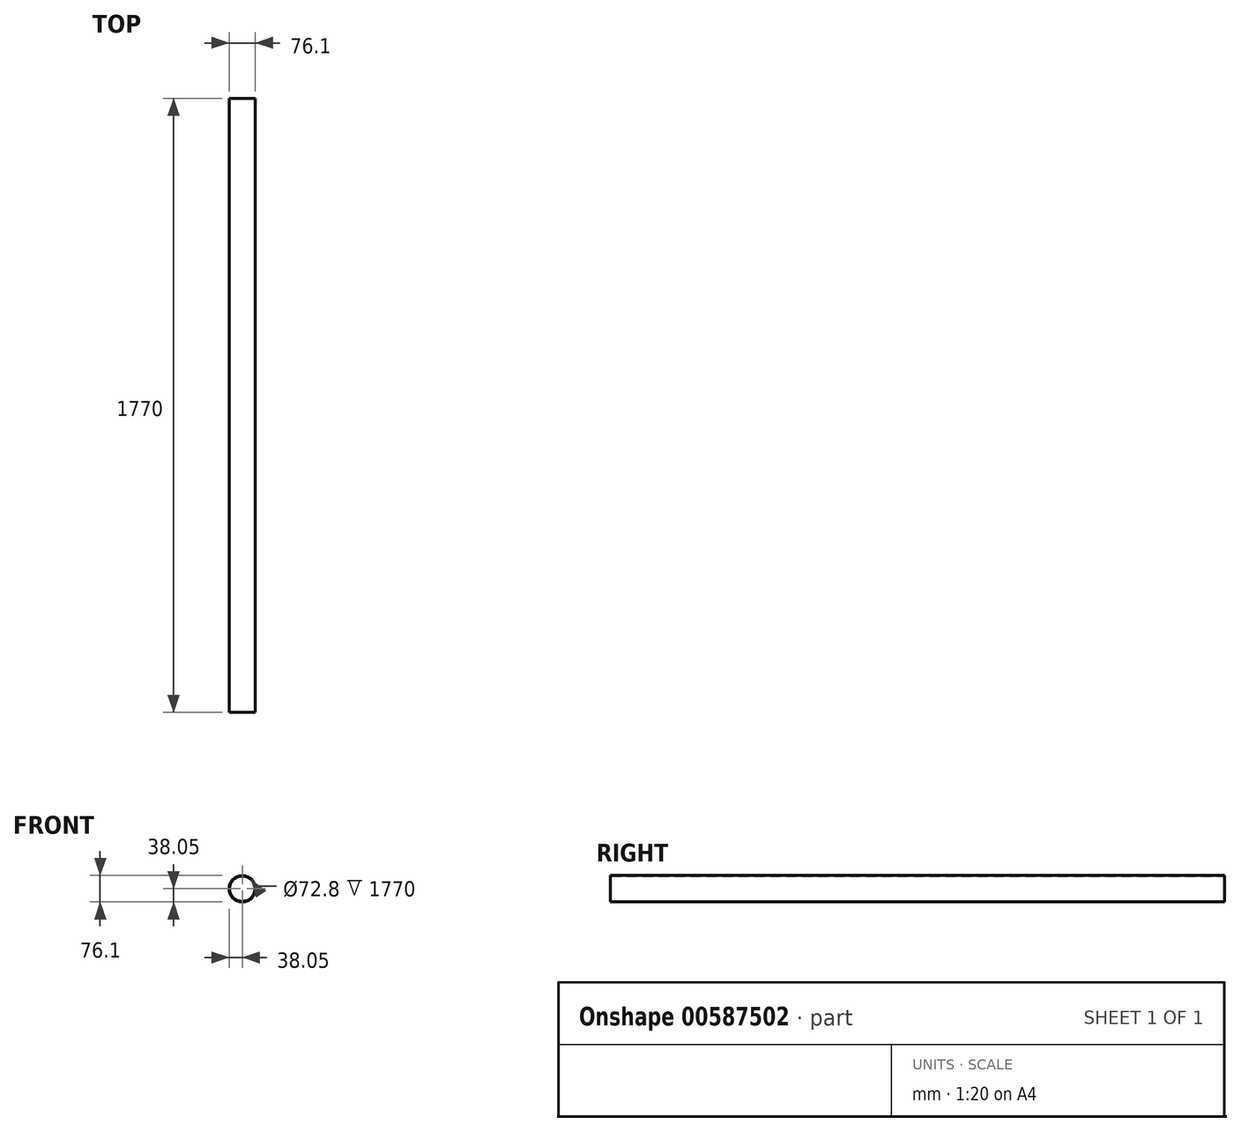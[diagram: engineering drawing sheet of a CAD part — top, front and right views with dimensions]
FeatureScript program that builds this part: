
annotation { "Feature Type Name" : "Feature", "Feature Type Description" : "" }
export const myFeature = defineFeature(function(context is Context, id is Id, definition is map)
    precondition{}
    {
        {
            var Q0;
            Q0=qCreatedBy(makeId("Front.planeOp"),FACE);
            var sketch = newSketch(context, id + "F0", { "sketchPlane" : qUnion([Q0])});
            skCircle(sketch, "E0", {"center": v(0, 0) * mm, "radius": 38.05 * mm});
            skCircle(sketch, "E1.0", {"center": v(0, 0) * mm, "radius": 36.4 * mm});
            skSolve(sketch);
        }
        {
            var Q0;
            Q0=makeQuery(id+"F0.imprint","IMPRINT",FACE,{"disambiguationData":[TD([[makeQuery(id+"F0.imprint","IMPRINT",EDGE,{"derivedFrom":sQuery(id+"F0.wireOp",EDGE,"E0")}),1.0]])]});
            var Q1;
            Q1=sQuery(id+"F0.wireOp",EDGE,"E0");
            var Q2;
            Q2=sQuery(id+"F0.wireOp",EDGE,"E1.0");
            extrude(context, id + "F1", {"entities" : qUnion([Q0]), "surfaceEntities" : qUnion([Q1, Q2]), "depth" : 1770 * mm, "offsetDistance" : 25 * mm});
        }
    });
